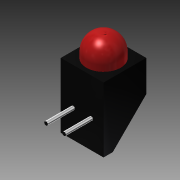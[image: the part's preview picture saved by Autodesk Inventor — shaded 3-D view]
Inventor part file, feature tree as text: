
AUTODESK INVENTOR PART (.ipt)
format: ipt  version: 2016 (Build 200138000, 138)  size: 117,248 bytes
history: native  units: mm
features: extrude x3, sketch x3, fillet x1
ambient origin geometry x8: Origin, YZ Plane, XZ Plane, XY Plane, X Axis, Y Axis, Z Axis, Center Point
bodies: Solid1 (feature_tree)
feature tree (7):
  extrude  "Extrusion1"  Depth=6.0mm
  extrude  "Extrusion2"  Depth=5.2mm
  fillet  "Fillet1"  Radius=1.3mm
  extrude  "Extrusion3"  Depth=6.0mm TaperAngle=0.0deg
  sketch  "Sketch1"  dims[d0=9.1mm d1=6.0mm]
  sketch  "Sketch2"  dims[d2=0.0mm d3=5.2mm d4=1.3mm]
  sketch  "Sketch3"  dims[d5=45.0deg d6=6.0mm d7=0.0mm d8=4.8mm d9=3.2mm d10=0.0mm d11=2.4mm d12=0.5mm d13=0.5mm d14=2.54mm d15=1.27mm d16=0.0mm d17=0.0mm d18=3.8mm d19=0.0mm]
